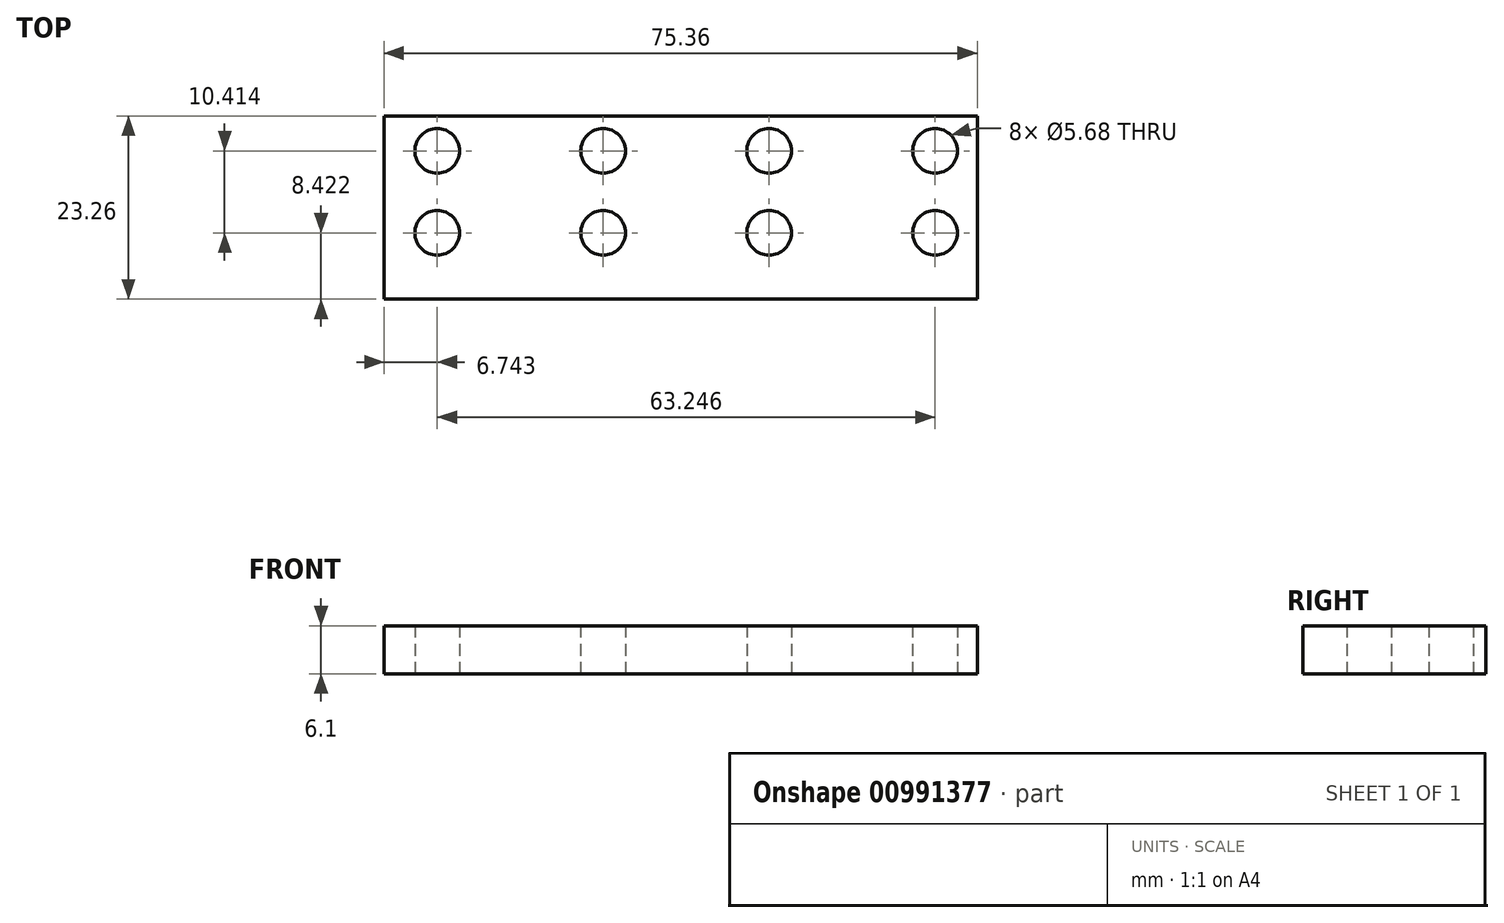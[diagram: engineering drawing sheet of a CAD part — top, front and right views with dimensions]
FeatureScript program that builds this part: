
annotation { "Feature Type Name" : "Feature", "Feature Type Description" : "" }
export const myFeature = defineFeature(function(context is Context, id is Id, definition is map)
    precondition{}
    {
        {
            var Q0;
            Q0=qCreatedBy(makeId("Top.planeOp"),FACE);
            var sketch = newSketch(context, id + "F0", { "sketchPlane" : qUnion([Q0])});
            skLineSegment(sketch, "E0.bottom", {"start": v(-41.98, 44.08) * mm, "end": v(33.38, 44.08) * mm});
            skLineSegment(sketch, "E0.top", {"start": v(-41.98, 20.82) * mm, "end": v(33.38, 20.82) * mm});
            skLineSegment(sketch, "E0.left", {"start": v(-41.98, 44.08) * mm, "end": v(-41.98, 20.82) * mm});
            skLineSegment(sketch, "E0.right", {"start": v(33.38, 44.08) * mm, "end": v(33.38, 20.82) * mm});
            skCircle(sketch, "E1", {"center": v(-35.24, 39.66) * mm, "radius": 2.84 * mm});
            skCircle(sketch, "E2.0.1.0", {"center": v(-35.24, 29.24) * mm, "radius": 2.84 * mm});
            skCircle(sketch, "E2.1.0.0", {"center": v(-14.15, 39.66) * mm, "radius": 2.84 * mm});
            skCircle(sketch, "E2.1.1.0", {"center": v(-14.15, 29.24) * mm, "radius": 2.84 * mm});
            skCircle(sketch, "E2.2.0.0", {"center": v(6.93, 39.66) * mm, "radius": 2.84 * mm});
            skCircle(sketch, "E2.2.1.0", {"center": v(6.93, 29.24) * mm, "radius": 2.84 * mm});
            skCircle(sketch, "E2.3.0.0", {"center": v(28, 39.66) * mm, "radius": 2.84 * mm});
            skCircle(sketch, "E2.3.1.0", {"center": v(28, 29.24) * mm, "radius": 2.84 * mm});
            skSolve(sketch);
        }
        {
            var Q0;
            Q0 = qSketchRegion(id + "F0", true);
            extrude(context, id + "F1", {"entities" : qUnion([Q0]), "depth" : 6.1 * mm, "offsetDistance" : 25.4 * mm});
        }
    });
